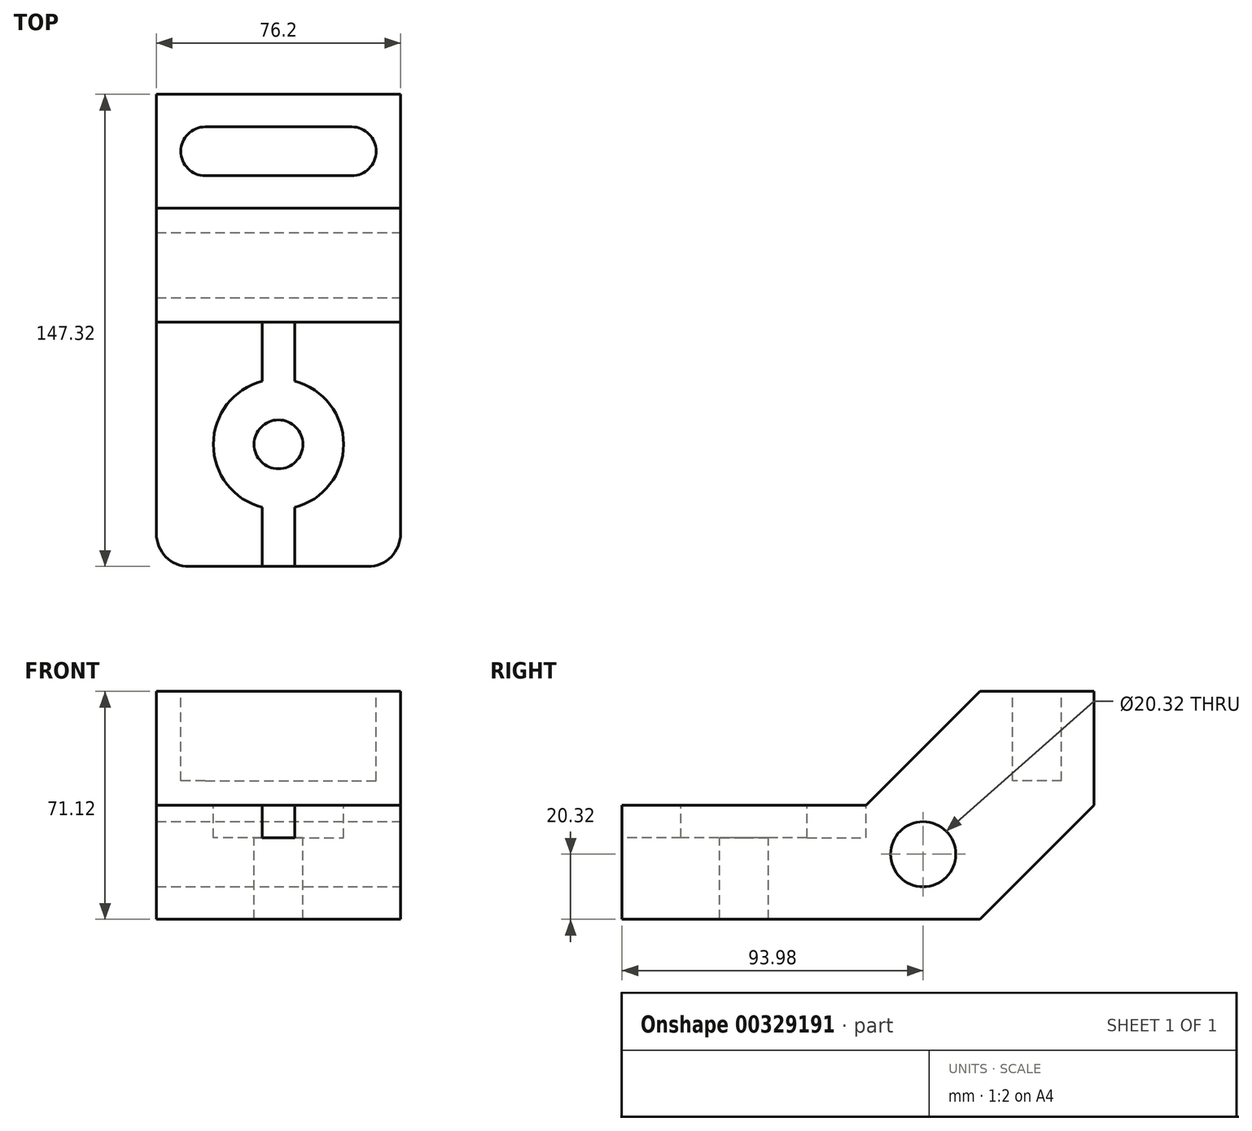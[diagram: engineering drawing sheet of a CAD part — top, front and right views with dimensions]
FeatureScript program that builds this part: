
annotation { "Feature Type Name" : "Feature", "Feature Type Description" : "" }
export const myFeature = defineFeature(function(context is Context, id is Id, definition is map)
    precondition{}
    {
        {
            var Q0;
            Q0=qCreatedBy(makeId("Front.planeOp"),FACE);
            var sketch = newSketch(context, id + "F0", { "sketchPlane" : qUnion([Q0])});
            skLineSegment(sketch, "E0.bottom", {"start": v(0, 0) * mm, "end": v(76.2, 0) * mm});
            skLineSegment(sketch, "E0.top", {"start": v(0, 71.12) * mm, "end": v(76.2, 71.12) * mm});
            skLineSegment(sketch, "E0.left", {"start": v(0, 0) * mm, "end": v(0, 71.12) * mm});
            skLineSegment(sketch, "E0.right", {"start": v(76.2, 0) * mm, "end": v(76.2, 71.12) * mm});
            skSolve(sketch);
        }
        {
            var Q0;
            Q0 = qSketchRegion(id + "F0", true);
            extrude(context, id + "F1", {"entities" : qUnion([Q0]), "depth" : 147.32 * mm});
        }
        {
            var Q0;
            Q0=makeQuery(id+"F1.opExtrude","SWEPT_FACE",FACE,{"disambiguationData":[OSD([sQuery(id+"F0.wireOp",EDGE,"E0.right")])]});
            var sketch = newSketch(context, id + "F2", { "sketchPlane" : qUnion([Q0])});
            skLineSegment(sketch, "E1", {"start": v(0, 35.56) * mm, "end": v(0, 0) * mm});
            skLineSegment(sketch, "E2", {"start": v(0, 0) * mm, "end": v(-35.56, 0) * mm});
            skLineSegment(sketch, "E3", {"start": v(-35.56, 0) * mm, "end": v(0, 35.56) * mm});
            skLineSegment(sketch, "E4", {"start": v(-35.56, 71.12) * mm, "end": v(-71.12, 35.56) * mm});
            skLineSegment(sketch, "E5", {"start": v(-71.12, 35.56) * mm, "end": v(-147.32, 35.56) * mm});
            skLineSegment(sketch, "E6", {"start": v(-147.32, 35.56) * mm, "end": v(-147.32, 71.12) * mm});
            skLineSegment(sketch, "E7", {"start": v(-147.32, 71.12) * mm, "end": v(-35.56, 71.12) * mm});
            skSolve(sketch);
        }
        {
            var Q0;
            Q0 = qSketchRegion(id + "F2", true);
            extrude(context, id + "F3", {"entities" : qUnion([Q0]), "operationType" : NewBodyOperationType.REMOVE, "endBound" : BoundingType.THROUGH_ALL, "oppositeDirection" : true, "depth" : 25.4 * mm});
        }
        {
            var Q0;
            Q0=makeQuery(id+"F1.opExtrude","CAP_EDGE",EDGE,{"disambiguationData":[OSD([sQuery(id+"F0.wireOp",EDGE,"E0.right")])],"isStart":false});
            var Q1;
            Q1=makeQuery(id+"F1.opExtrude","CAP_EDGE",EDGE,{"disambiguationData":[OSD([sQuery(id+"F0.wireOp",EDGE,"E0.left")])],"isStart":false});
            fillet(context, id + "F4", {"entities" : qUnion([Q0, Q1]), "radius" : 10.16 * mm, "tangentPropagation" : true, "allowEdgeOverflow" : false});
        }
        {
            var Q0;
            Q0=makeQuery(id+"F1.opExtrude","SWEPT_FACE",FACE,{"disambiguationData":[OSD([sQuery(id+"F0.wireOp",EDGE,"E0.top")])]});
            var sketch = newSketch(context, id + "F5", { "sketchPlane" : qUnion([Q0])});
            skLineSegment(sketch, "E8", {"start": v(15.24, -10.16) * mm, "end": v(60.96, -10.16) * mm});
            skLineSegment(sketch, "E9", {"start": v(15.24, -25.4) * mm, "end": v(60.96, -25.4) * mm});
            skArc(sketch, "E10", {"start": v(15.24, -10.16) * mm, "mid": v(7.62, -17.78) * mm, "end": v(15.24, -25.4) * mm});
            skArc(sketch, "E11", {"start": v(60.96, -10.16) * mm, "mid": v(68.58, -17.78) * mm, "end": v(60.96, -25.4) * mm});
            skLineSegment(sketch, "E12", {"start": v(38.1, -25.4) * mm, "end": v(38.1, -10.16) * mm, "construction": true});
            skSolve(sketch);
        }
        {
            var Q0;
            Q0 = qSketchRegion(id + "F5", true);
            extrude(context, id + "F6", {"entities" : qUnion([Q0]), "operationType" : NewBodyOperationType.REMOVE, "oppositeDirection" : true, "depth" : 27.94 * mm});
        }
        {
            var Q0;
            Q0=makeQuery(id+"F1.opExtrude","SWEPT_FACE",FACE,{"disambiguationData":[OSD([sQuery(id+"F0.wireOp",EDGE,"E0.right")])]});
            var sketch = newSketch(context, id + "F7", { "sketchPlane" : qUnion([Q0])});
            skCircle(sketch, "E13", {"center": v(-53.34, 20.32) * mm, "radius": 10.16 * mm});
            skSolve(sketch);
        }
        {
            var Q0;
            Q0 = qSketchRegion(id + "F7", true);
            extrude(context, id + "F8", {"entities" : qUnion([Q0]), "operationType" : NewBodyOperationType.REMOVE, "endBound" : BoundingType.THROUGH_ALL, "oppositeDirection" : true, "depth" : 25.4 * mm});
        }
        {
            var Q0;
            Q0=makeQuery(id+"F3.boolean.opBoolean","COPY",FACE,{"derivedFrom":makeQuery(id+"F3.opExtrude","SWEPT_FACE",FACE,{"disambiguationData":[OSD([sQuery(id+"F2.wireOp",EDGE,"E5")])]})});
            var sketch = newSketch(context, id + "F9", { "sketchPlane" : qUnion([Q0])});
            skArc(sketch, "E14", {"start": v(33.02, -89.55) * mm, "mid": v(17.78, -109.22) * mm, "end": v(33.02, -128.9) * mm});
            skPoint(sketch, "E14.centerSnap0", {"position": v(38.1, -71.12) * mm});
            skLineSegment(sketch, "E15", {"start": v(43.18, -128.9) * mm, "end": v(43.18, -147.32) * mm});
            skLineSegment(sketch, "E16", {"start": v(33.02, -128.9) * mm, "end": v(33.02, -147.32) * mm});
            skLineSegment(sketch, "E17", {"start": v(43.18, -89.55) * mm, "end": v(43.18, -71.12) * mm});
            skLineSegment(sketch, "E18", {"start": v(33.02, -89.55) * mm, "end": v(33.02, -71.12) * mm});
            skArc(sketch, "E19.trimOffspring", {"start": v(43.18, -128.9) * mm, "mid": v(58.42, -109.22) * mm, "end": v(43.18, -89.55) * mm});
            skLineSegment(sketch, "E20", {"start": v(33.02, -71.12) * mm, "end": v(43.18, -71.12) * mm});
            skLineSegment(sketch, "E21", {"start": v(33.02, -147.32) * mm, "end": v(43.18, -147.32) * mm});
            skSolve(sketch);
        }
        {
            var Q0;
            Q0 = qSketchRegion(id + "F9", true);
            extrude(context, id + "F10", {"entities" : qUnion([Q0]), "operationType" : NewBodyOperationType.REMOVE, "oppositeDirection" : true, "depth" : 10.16 * mm});
        }
        {
            var Q0;
            Q0=makeQuery(id+"F10.boolean.opBoolean","COPY",FACE,{"derivedFrom":makeQuery(id+"F10.opExtrude","CAP_FACE",FACE,{"disambiguationData":[OSD([sQuery(id+"F9.wireOp",EDGE,"E14"),sQuery(id+"F9.wireOp",EDGE,"E15"),sQuery(id+"F9.wireOp",EDGE,"E16"),sQuery(id+"F9.wireOp",EDGE,"E17"),sQuery(id+"F9.wireOp",EDGE,"E18"),sQuery(id+"F9.wireOp",EDGE,"E19.trimOffspring"),sQuery(id+"F9.wireOp",EDGE,"E20"),sQuery(id+"F9.wireOp",EDGE,"E21")])],"isStart":false})});
            var sketch = newSketch(context, id + "F11", { "sketchPlane" : qUnion([Q0])});
            skCircle(sketch, "E22", {"center": v(38.1, -109.22) * mm, "radius": 7.62 * mm});
            skSolve(sketch);
        }
        {
            var Q0;
            Q0 = qSketchRegion(id + "F11", true);
            extrude(context, id + "F12", {"entities" : qUnion([Q0]), "operationType" : NewBodyOperationType.REMOVE, "endBound" : BoundingType.THROUGH_ALL, "oppositeDirection" : true, "depth" : 25.4 * mm});
        }
    });
